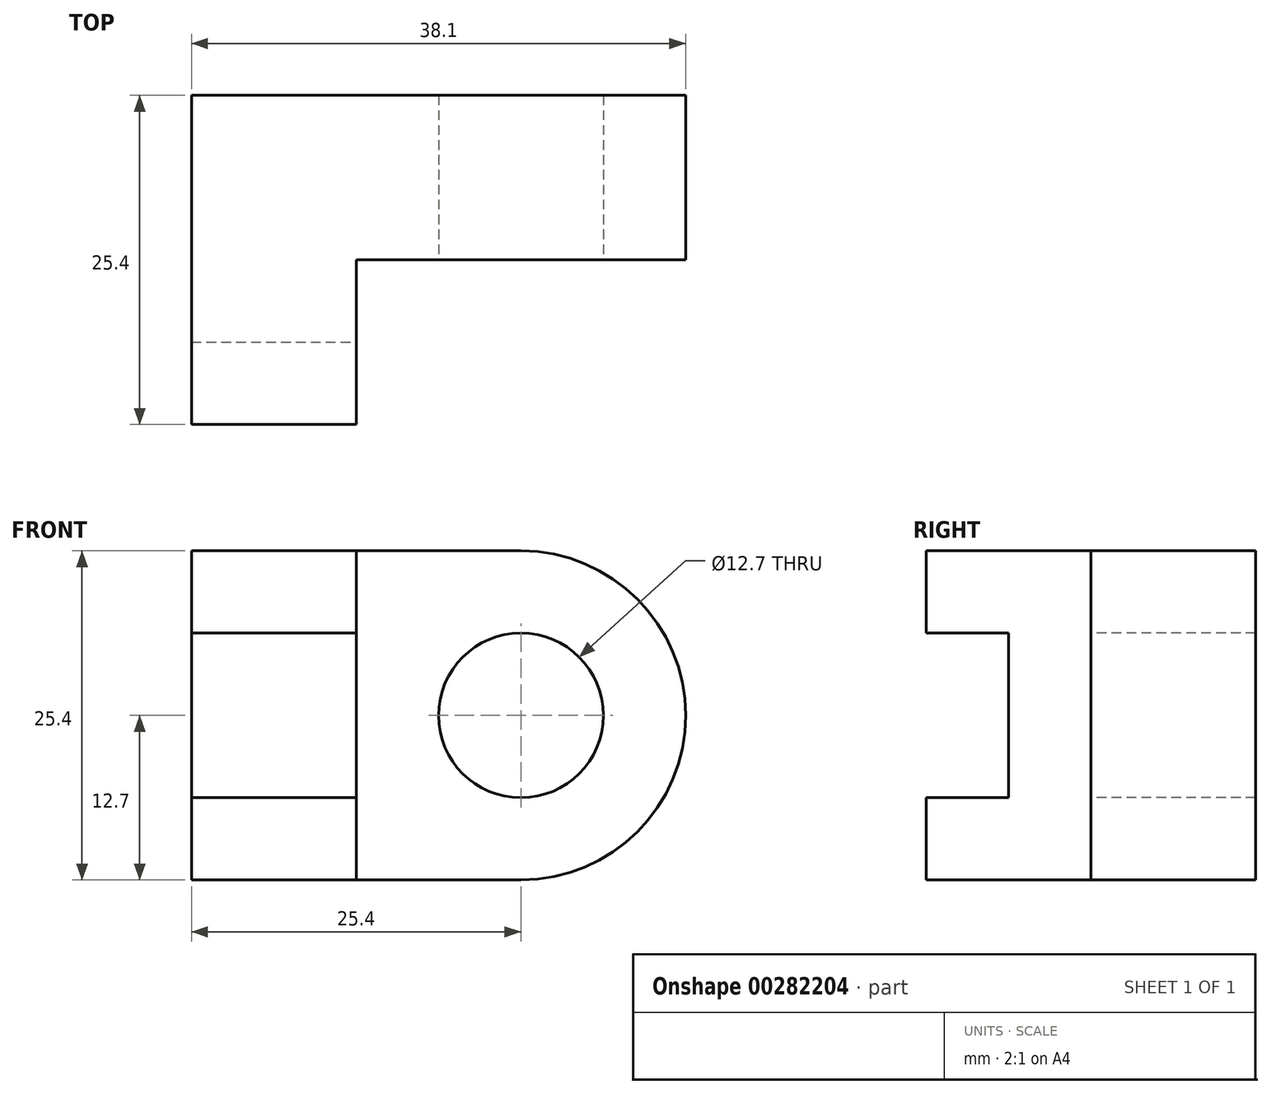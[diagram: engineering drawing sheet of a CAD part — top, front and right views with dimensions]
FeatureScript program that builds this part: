
annotation { "Feature Type Name" : "Feature", "Feature Type Description" : "" }
export const myFeature = defineFeature(function(context is Context, id is Id, definition is map)
    precondition{}
    {
        {
            var Q0;
            Q0=qCreatedBy(makeId("Front.planeOp"),FACE);
            var sketch = newSketch(context, id + "F0", { "sketchPlane" : qUnion([Q0])});
            skLineSegment(sketch, "E0.bottom", {"start": v(0, 0) * mm, "end": v(25.4, 0) * mm});
            skLineSegment(sketch, "E0.top", {"start": v(0, 25.4) * mm, "end": v(25.4, 25.4) * mm});
            skLineSegment(sketch, "E0.left", {"start": v(0, 0) * mm, "end": v(0, 25.4) * mm});
            skLineSegment(sketch, "E0.right", {"start": v(25.4, 0) * mm, "end": v(25.4, 25.4) * mm});
            skSolve(sketch);
        }
        {
            var Q0;
            Q0 = qSketchRegion(id + "F0", true);
            extrude(context, id + "F1", {"entities" : qUnion([Q0]), "depth" : 12.7 * mm});
        }
        {
            var Q0;
            Q0=makeQuery(id+"F1.opExtrude","CAP_FACE",FACE,{"disambiguationData":[OSD([sQuery(id+"F0.wireOp",EDGE,"E0.bottom"),sQuery(id+"F0.wireOp",EDGE,"E0.top"),sQuery(id+"F0.wireOp",EDGE,"E0.left"),sQuery(id+"F0.wireOp",EDGE,"E0.right")])],"isStart":false});
            var sketch = newSketch(context, id + "F2", { "sketchPlane" : qUnion([Q0])});
            skLineSegment(sketch, "E1.bottom", {"start": v(0, 25.4) * mm, "end": v(12.7, 25.4) * mm});
            skLineSegment(sketch, "E1.top", {"start": v(0, 0) * mm, "end": v(12.7, 0) * mm});
            skLineSegment(sketch, "E1.left", {"start": v(0, 25.4) * mm, "end": v(0, 0) * mm});
            skLineSegment(sketch, "E1.right", {"start": v(12.7, 25.4) * mm, "end": v(12.7, 0) * mm});
            skSolve(sketch);
        }
        {
            var Q0;
            Q0 = qSketchRegion(id + "F2", true);
            extrude(context, id + "F3", {"entities" : qUnion([Q0]), "operationType" : NewBodyOperationType.ADD, "depth" : 12.7 * mm});
        }
        {
            var Q0;
            Q0=makeQuery(id+"F3.opExtrude","CAP_FACE",FACE,{"disambiguationData":[OSD([sQuery(id+"F2.wireOp",EDGE,"E1.bottom"),sQuery(id+"F2.wireOp",EDGE,"E1.top"),sQuery(id+"F2.wireOp",EDGE,"E1.left"),sQuery(id+"F2.wireOp",EDGE,"E1.right")])],"isStart":false});
            var sketch = newSketch(context, id + "F4", { "sketchPlane" : qUnion([Q0])});
            skLineSegment(sketch, "E2.bottom", {"start": v(0, 19.05) * mm, "end": v(12.7, 19.05) * mm});
            skLineSegment(sketch, "E2.top", {"start": v(0, 6.35) * mm, "end": v(12.7, 6.35) * mm});
            skLineSegment(sketch, "E2.left", {"start": v(0, 19.05) * mm, "end": v(0, 6.35) * mm});
            skLineSegment(sketch, "E2.right", {"start": v(12.7, 19.05) * mm, "end": v(12.7, 6.35) * mm});
            skSolve(sketch);
        }
        {
            var Q0;
            Q0 = qSketchRegion(id + "F4", true);
            extrude(context, id + "F5", {"entities" : qUnion([Q0]), "operationType" : NewBodyOperationType.REMOVE, "oppositeDirection" : true, "depth" : 6.35 * mm});
        }
        {
            var Q0;
            Q0=qCreatedBy(makeId("Front.planeOp"),FACE);
            var sketch = newSketch(context, id + "F6", { "sketchPlane" : qUnion([Q0])});
            skArc(sketch, "E3", {"start": v(25.4, 0) * mm, "mid": v(38.1, 12.7) * mm, "end": v(25.4, 25.4) * mm});
            skLineSegment(sketch, "E4", {"start": v(25.4, 25.4) * mm, "end": v(25.4, 0) * mm});
            skSolve(sketch);
        }
        {
            var Q0;
            Q0 = qSketchRegion(id + "F6", true);
            extrude(context, id + "F7", {"entities" : qUnion([Q0]), "operationType" : NewBodyOperationType.ADD, "depth" : 12.7 * mm});
        }
        {
            var Q0;
            Q0=makeQuery(id+"F7.boolean.opBoolean","MERGE",FACE,{"derivedFrom":[makeQuery(id+"F1.opExtrude","CAP_FACE",FACE,{"disambiguationData":[OSD([sQuery(id+"F0.wireOp",EDGE,"E0.bottom"),sQuery(id+"F0.wireOp",EDGE,"E0.top"),sQuery(id+"F0.wireOp",EDGE,"E0.left"),sQuery(id+"F0.wireOp",EDGE,"E0.right")])],"isStart":false}),makeQuery(id+"F7.opExtrude","CAP_FACE",FACE,{"disambiguationData":[OSD([sQuery(id+"F6.wireOp",EDGE,"E3"),sQuery(id+"F6.wireOp",EDGE,"E4")])],"isStart":false})]});
            var sketch = newSketch(context, id + "F8", { "sketchPlane" : qUnion([Q0])});
            skCircle(sketch, "E5", {"center": v(25.4, 12.7) * mm, "radius": 6.35 * mm});
            skSolve(sketch);
        }
        {
            var Q0;
            Q0 = qSketchRegion(id + "F8", true);
            extrude(context, id + "F9", {"entities" : qUnion([Q0]), "operationType" : NewBodyOperationType.REMOVE, "oppositeDirection" : true, "depth" : 12.7 * mm});
        }
    });
